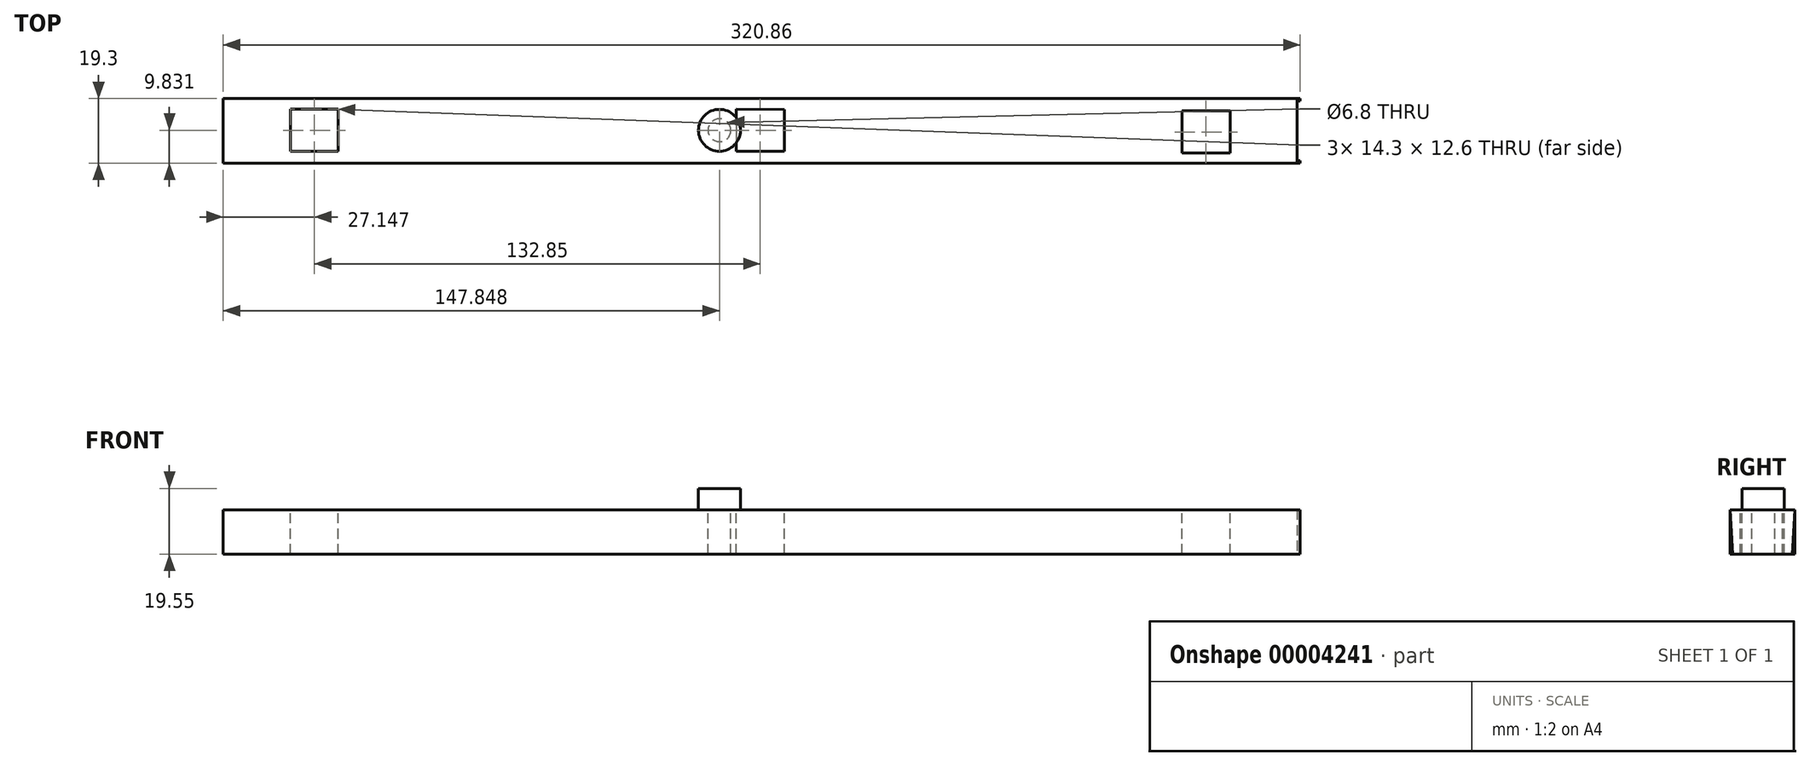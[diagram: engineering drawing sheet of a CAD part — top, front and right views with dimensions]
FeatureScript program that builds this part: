
annotation { "Feature Type Name" : "Feature", "Feature Type Description" : "" }
export const myFeature = defineFeature(function(context is Context, id is Id, definition is map)
    precondition{}
    {
        {
            var Q0;
            Q0=qCreatedBy(makeId("Top.planeOp"),FACE);
            var sketch = newSketch(context, id + "F0", { "sketchPlane" : qUnion([Q0])});
            skLineSegment(sketch, "E0.bottom", {"start": v(-114.47, 0) * mm, "end": v(205.53, 0) * mm});
            skLineSegment(sketch, "E0.top", {"start": v(-114.47, -19.3) * mm, "end": v(205.53, -19.3) * mm});
            skLineSegment(sketch, "E0.left", {"start": v(-114.47, 0) * mm, "end": v(-114.47, -19.3) * mm});
            skLineSegment(sketch, "E0.right", {"start": v(205.53, 0) * mm, "end": v(205.53, -19.3) * mm});
            skLineSegment(sketch, "E1.bottom", {"start": v(-94.47, -3.17) * mm, "end": v(-80.17, -3.17) * mm});
            skLineSegment(sketch, "E1.top", {"start": v(-94.47, -15.77) * mm, "end": v(-80.17, -15.77) * mm});
            skLineSegment(sketch, "E1.left", {"start": v(-94.47, -3.17) * mm, "end": v(-94.47, -15.77) * mm});
            skLineSegment(sketch, "E1.right", {"start": v(-80.17, -3.17) * mm, "end": v(-80.17, -15.77) * mm});
            skLineSegment(sketch, "E2.bottom", {"start": v(171.23, -3.66) * mm, "end": v(185.53, -3.66) * mm});
            skLineSegment(sketch, "E2.top", {"start": v(171.23, -16.26) * mm, "end": v(185.53, -16.26) * mm});
            skLineSegment(sketch, "E2.left", {"start": v(171.23, -3.66) * mm, "end": v(171.23, -16.26) * mm});
            skLineSegment(sketch, "E2.right", {"start": v(185.53, -3.66) * mm, "end": v(185.53, -16.26) * mm});
            skLineSegment(sketch, "E3.bottom", {"start": v(38.38, -3.17) * mm, "end": v(52.68, -3.25) * mm});
            skLineSegment(sketch, "E3.top", {"start": v(38.38, -15.77) * mm, "end": v(52.68, -15.77) * mm});
            skLineSegment(sketch, "E3.left", {"start": v(38.38, -3.17) * mm, "end": v(38.38, -15.77) * mm});
            skLineSegment(sketch, "E3.right", {"start": v(52.68, -3.25) * mm, "end": v(52.68, -15.77) * mm});
            skCircle(sketch, "E4", {"center": v(33.38, -9.47) * mm, "radius": 3.4 * mm});
            skLineSegment(sketch, "E5", {"start": v(-80.17, -3.17) * mm, "end": v(38.38, -3.17) * mm});
            skLineSegment(sketch, "E6", {"start": v(52.68, -3.25) * mm, "end": v(171.23, -3.66) * mm});
            skLineSegment(sketch, "E7", {"start": v(33.38, -9.47) * mm, "end": v(38.38, -9.47) * mm});
            skSolve(sketch);
        }
        {
            var Q0;
            Q0=makeQuery(id+"F0.imprint","IMPRINT",FACE,{"disambiguationData":[TD([[makeQuery(id+"F0.imprint","IMPRINT",EDGE,{"derivedFrom":sQuery(id+"F0.wireOp",EDGE,"E0.bottom")}),-1.0]])]});
            extrude(context, id + "F1", {"entities" : qUnion([Q0]), "oppositeDirection" : true, "depth" : 13.2 * mm});
        }
        {
            var Q0;
            Q0=makeQuery(id+"F1.opExtrude","SWEPT_FACE",FACE,{"disambiguationData":[OSD([sQuery(id+"F0.wireOp",EDGE,"E0.left")])]});
            var sketch = newSketch(context, id + "F2", { "sketchPlane" : qUnion([Q0])});
            skLineSegment(sketch, "E8", {"start": v(0, 0) * mm, "end": v(0.75, -13.2) * mm});
            skLineSegment(sketch, "E9", {"start": v(0.75, -13.2) * mm, "end": v(0, -13.2) * mm});
            skLineSegment(sketch, "E10", {"start": v(0, -13.2) * mm, "end": v(0, 0) * mm});
            skLineSegment(sketch, "E11", {"start": v(19.3, 0) * mm, "end": v(18.55, -13.2) * mm});
            skLineSegment(sketch, "E12", {"start": v(18.55, -13.2) * mm, "end": v(19.3, -13.2) * mm});
            skLineSegment(sketch, "E13", {"start": v(19.3, -13.2) * mm, "end": v(19.3, 0) * mm});
            skLineSegment(sketch, "E14", {"start": v(0.75, -13.2) * mm, "end": v(18.55, -13.2) * mm});
            skSolve(sketch);
        }
        {
            var Q0;
            Q0=makeQuery(id+"F2.imprint","IMPRINT",FACE,{"disambiguationData":[TD([[makeQuery(id+"F2.imprint","IMPRINT",EDGE,{"derivedFrom":sQuery(id+"F2.wireOp",EDGE,"E8")}),-1.0]])]});
            var Q1;
            Q1=makeQuery(id+"F2.imprint","IMPRINT",FACE,{"disambiguationData":[TD([[makeQuery(id+"F2.imprint","IMPRINT",EDGE,{"derivedFrom":sQuery(id+"F2.wireOp",EDGE,"E11")}),1.0]])]});
            extrude(context, id + "F3", {"entities" : qUnion([Q0, Q1]), "operationType" : NewBodyOperationType.ADD, "endBound" : BoundingType.THROUGH_ALL, "oppositeDirection" : true, "depth" : 25 * mm});
        }
        {
            var Q0;
            Q0=qCreatedBy(makeId("Top.planeOp"),FACE);
            var sketch = newSketch(context, id + "F4", { "sketchPlane" : qUnion([Q0])});
            skCircle(sketch, "E15", {"center": v(33.37, -9.48) * mm, "radius": 6.25 * mm});
            skSolve(sketch);
        }
        {
            var Q0;
            Q0=makeQuery(id+"F4.imprint","IMPRINT",FACE,{"disambiguationData":[TD([[makeQuery(id+"F4.imprint","IMPRINT",EDGE,{"derivedFrom":sQuery(id+"F4.wireOp",EDGE,"E15")}),1.0]])]});
            extrude(context, id + "F5", {"entities" : qUnion([Q0]), "depth" : 6.35 * mm});
        }
    });
